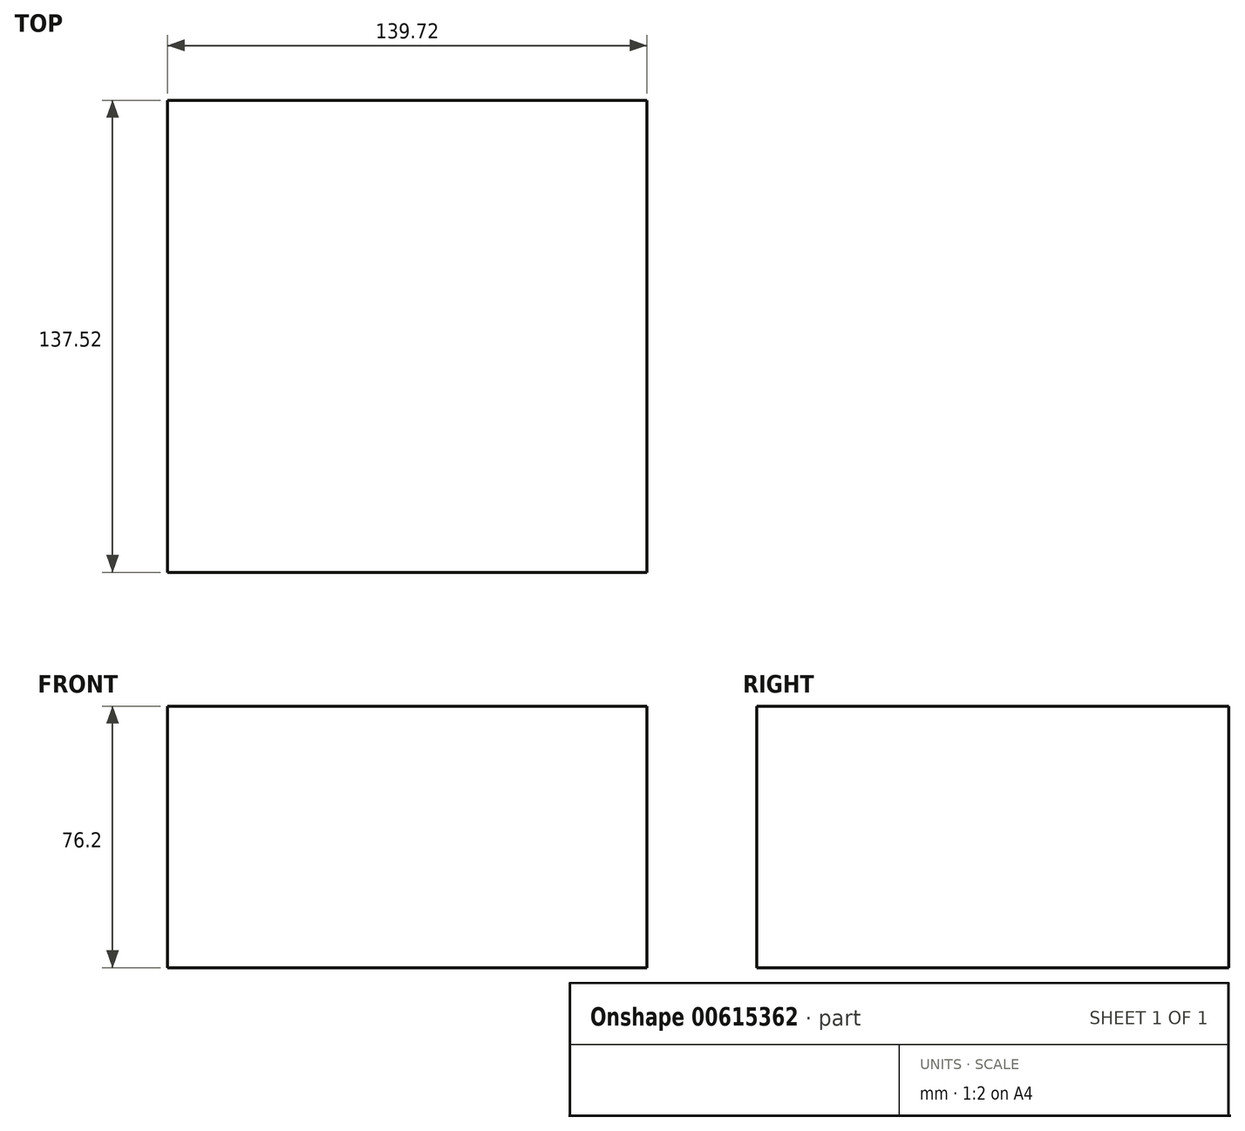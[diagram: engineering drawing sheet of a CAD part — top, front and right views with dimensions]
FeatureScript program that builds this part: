
annotation { "Feature Type Name" : "Feature", "Feature Type Description" : "" }
export const myFeature = defineFeature(function(context is Context, id is Id, definition is map)
    precondition{}
    {
        {
            var Q0;
            Q0=qCreatedBy(makeId("Top.planeOp"),FACE);
            var sketch = newSketch(context, id + "F0", { "sketchPlane" : qUnion([Q0])});
            skLineSegment(sketch, "E0.bottom", {"start": v(69.86, -68.76) * mm, "end": v(-69.86, -68.76) * mm});
            skLineSegment(sketch, "E0.top", {"start": v(69.86, 68.76) * mm, "end": v(-69.86, 68.76) * mm});
            skLineSegment(sketch, "E0.left", {"start": v(69.86, -68.76) * mm, "end": v(69.86, 68.76) * mm});
            skLineSegment(sketch, "E0.right", {"start": v(-69.86, -68.76) * mm, "end": v(-69.86, 68.76) * mm});
            skPoint(sketch, "E0.middle", {"position": v(0, 0) * mm});
            skLineSegment(sketch, "E1", {"start": v(0, 68.76) * mm, "end": v(0, -68.76) * mm});
            skSolve(sketch);
        }
        {
            var Q0;
            Q0=qCreatedBy(makeId("Top.planeOp"),FACE);
            var sketch = newSketch(context, id + "F1", { "sketchPlane" : qUnion([Q0])});
            skCircle(sketch, "E2", {"center": v(54.26, 0) * mm, "radius": 9.82 * mm});
            skSolve(sketch);
        }
        {
            var Q0;
            {var subQ0=sQuery(id+"F0.wireOp",EDGE,"E0.left");Q0=makeQuery(id+"F0.imprint","IMPRINT",FACE,{"disambiguationData":[TD([[makeQuery(id+"F0.imprint","IMPRINT",EDGE,{"derivedFrom":subQ0}),1.0]])]});}
            extrude(context, id + "F2", {"entities" : qUnion([Q0]), "oppositeDirection" : true, "depth" : 76.2 * mm, "offsetDistance" : 25.4 * mm});
        }
        {
            var Q0;
            {var subQ0=sQuery(id+"F0.wireOp",EDGE,"E0.right");Q0=makeQuery(id+"F0.imprint","IMPRINT",FACE,{"disambiguationData":[TD([[makeQuery(id+"F0.imprint","IMPRINT",EDGE,{"derivedFrom":subQ0}),-1.0]])]});}
            extrude(context, id + "F3", {"entities" : qUnion([Q0]), "operationType" : NewBodyOperationType.ADD, "oppositeDirection" : true, "depth" : 76.2 * mm, "offsetDistance" : 25.4 * mm});
        }
        {
            var Q0;
            Q0=sQuery(id+"F1.wireOp",EDGE,"E2");
            var Q1;
            Q1=sQuery(id+"F0.wireOp",EDGE,"E1");
            revolve(context, id + "F4", {"bodyType" : ToolBodyType.SURFACE, "surfaceEntities" : qUnion([Q0]), "axis" : qUnion([Q1]), "revolveType" : RevolveType.FULL});
        }
    });
